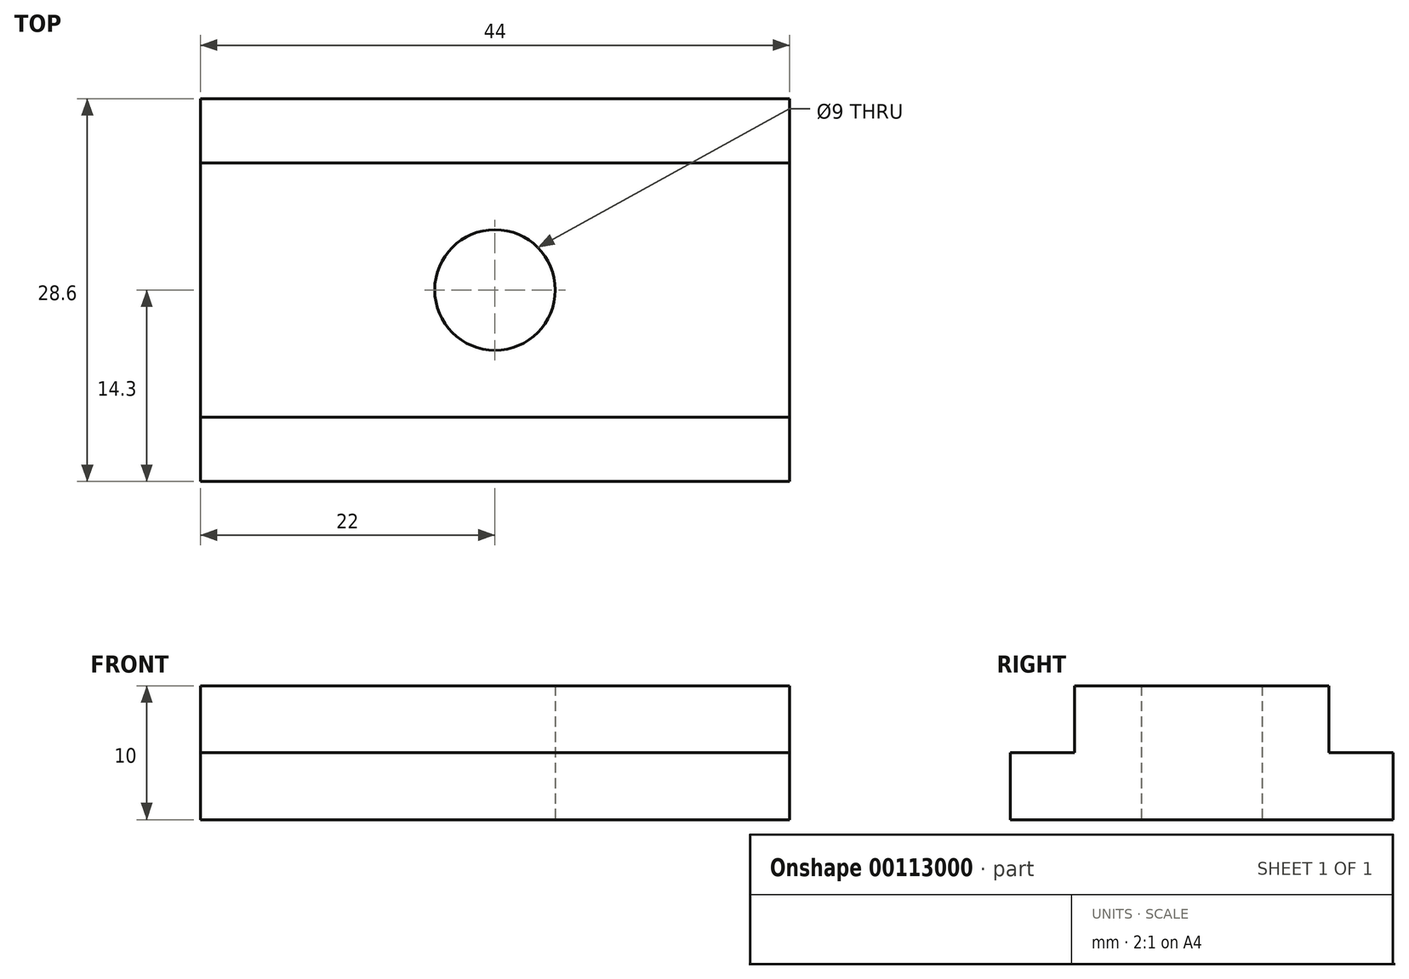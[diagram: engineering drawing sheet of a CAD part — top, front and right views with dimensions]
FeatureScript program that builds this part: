
annotation { "Feature Type Name" : "Feature", "Feature Type Description" : "" }
export const myFeature = defineFeature(function(context is Context, id is Id, definition is map)
    precondition{}
    {
        {
            var Q0;
            Q0=qCreatedBy(makeId("Top.planeOp"),FACE);
            var sketch = newSketch(context, id + "F0", { "sketchPlane" : qUnion([Q0])});
            skLineSegment(sketch, "E0.bottom", {"start": v(0, 0) * mm, "end": v(44, 0) * mm});
            skLineSegment(sketch, "E0.top", {"start": v(0, 28.6) * mm, "end": v(44, 28.6) * mm});
            skLineSegment(sketch, "E0.left", {"start": v(0, 0) * mm, "end": v(0, 28.6) * mm});
            skLineSegment(sketch, "E0.right", {"start": v(44, 0) * mm, "end": v(44, 28.6) * mm});
            skLineSegment(sketch, "E1", {"start": v(22, 28.6) * mm, "end": v(22, 0) * mm, "construction": true});
            skLineSegment(sketch, "E2", {"start": v(0, 14.3) * mm, "end": v(44, 14.3) * mm, "construction": true});
            skCircle(sketch, "E3", {"center": v(22, 14.3) * mm, "radius": 4.5 * mm});
            skLineSegment(sketch, "E4", {"start": v(0, 23.8) * mm, "end": v(44, 23.8) * mm});
            skLineSegment(sketch, "E5", {"start": v(0, 4.8) * mm, "end": v(44, 4.8) * mm});
            skSolve(sketch);
        }
        {
            var Q0;
            Q0=makeQuery(id+"F0.imprint","IMPRINT",FACE,{"disambiguationData":[TD([[makeQuery(id+"F0.imprint","IMPRINT",EDGE,{"derivedFrom":sQuery(id+"F0.wireOp",EDGE,"E3")}),-1.0]])]});
            extrude(context, id + "F1", {"entities" : qUnion([Q0]), "depth" : 10 * mm});
        }
        {
            var Q0;
            {var subQ0=sQuery(id+"F0.wireOp",EDGE,"E0.bottom");Q0=makeQuery(id+"F0.imprint","IMPRINT",FACE,{"disambiguationData":[TD([[makeQuery(id+"F0.imprint","IMPRINT",EDGE,{"derivedFrom":subQ0}),1.0]])]});}
            var Q1;
            {var subQ0=sQuery(id+"F0.wireOp",EDGE,"E0.top");Q1=makeQuery(id+"F0.imprint","IMPRINT",FACE,{"disambiguationData":[TD([[makeQuery(id+"F0.imprint","IMPRINT",EDGE,{"derivedFrom":subQ0}),-1.0]])]});}
            extrude(context, id + "F2", {"entities" : qUnion([Q0, Q1]), "operationType" : NewBodyOperationType.ADD, "depth" : 5 * mm});
        }
    });
